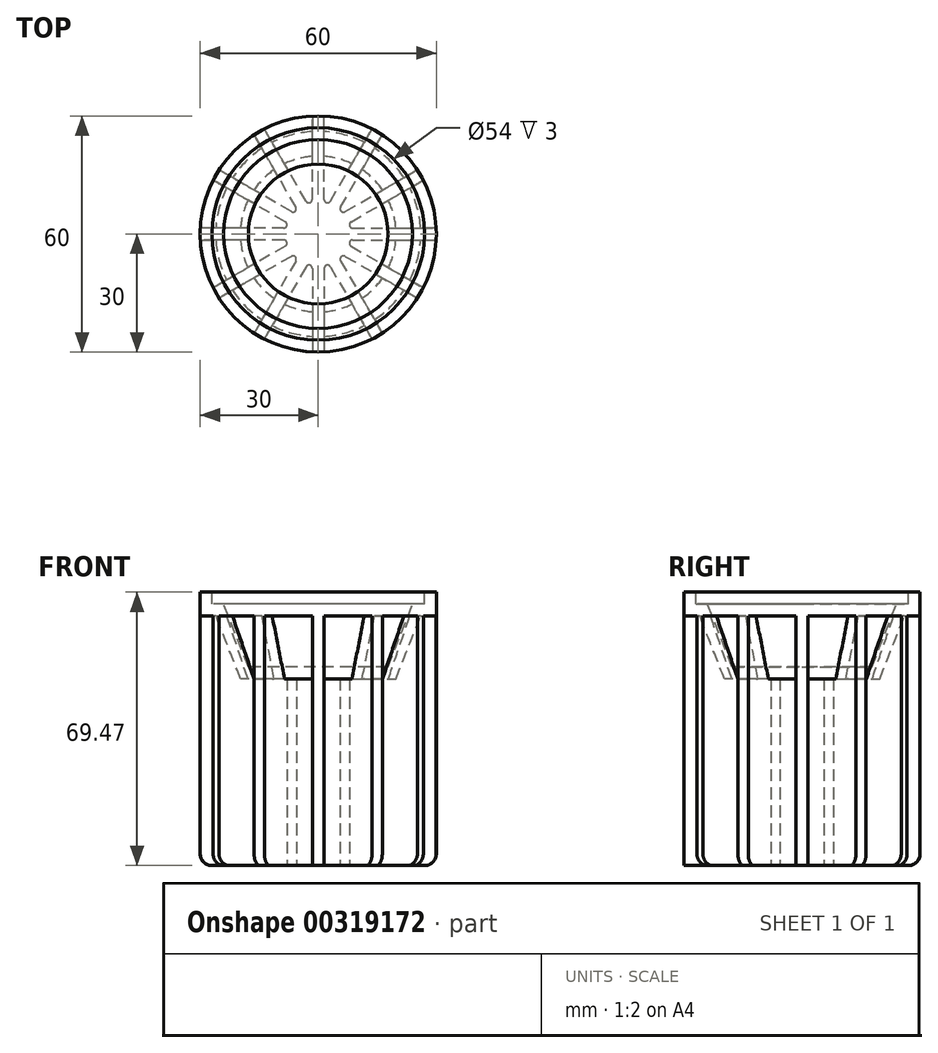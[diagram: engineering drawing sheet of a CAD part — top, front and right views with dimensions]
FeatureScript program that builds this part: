
annotation { "Feature Type Name" : "Feature", "Feature Type Description" : "" }
export const myFeature = defineFeature(function(context is Context, id is Id, definition is map)
    precondition{}
    {
        {
            var Q0;
            Q0=qCreatedBy(makeId("Right.planeOp"),FACE);
            var sketch = newSketch(context, id + "F0", { "sketchPlane" : qUnion([Q0])});
            skLineSegment(sketch, "E0", {"start": v(0, -12.53) * mm, "end": v(-19.8, -12.53) * mm});
            skLineSegment(sketch, "E1", {"start": v(-19.8, -12.53) * mm, "end": v(-26.05, 3.47) * mm});
            skLineSegment(sketch, "E2", {"start": v(-26.05, 3.47) * mm, "end": v(-30, 3.47) * mm});
            skLineSegment(sketch, "E3", {"start": v(-30, 3.47) * mm, "end": v(-30, 9.47) * mm});
            skLineSegment(sketch, "E4", {"start": v(-30, 9.47) * mm, "end": v(-27, 9.47) * mm});
            skLineSegment(sketch, "E5.0", {"start": v(-17.74, -9.53) * mm, "end": v(-24, 6.47) * mm});
            skLineSegment(sketch, "E6.0", {"start": v(0, -9.53) * mm, "end": v(-17.74, -9.53) * mm});
            skLineSegment(sketch, "E7", {"start": v(-24, 6.47) * mm, "end": v(-27, 6.47) * mm});
            skLineSegment(sketch, "E8", {"start": v(-27, 6.47) * mm, "end": v(-27, 9.47) * mm});
            skLineSegment(sketch, "E9", {"start": v(0, -9.53) * mm, "end": v(0, -12.53) * mm});
            skSolve(sketch);
        }
        {
            var Q0;
            Q0 = qSketchRegion(id + "F0", true);
            var Q1;
            Q1=sQuery(id+"F0.wireOp",EDGE,"E9");
            revolve(context, id + "F1", {"entities" : qUnion([Q0]), "axis" : qUnion([Q1]), "revolveType" : RevolveType.FULL});
        }
        {
            var Q0;
            Q0=qCreatedBy(makeId("Top.planeOp"),FACE);
            cPlane(context, id + "F2", {"entities" : qUnion([Q0]), "cplaneType" : CPlaneType.OFFSET, "offset" : 60 * mm, "oppositeDirection" : true, "width" : 150 * mm, "height" : 150 * mm});
        }
        {
            var Q0;
            Q0=qCreatedBy(id+"F2.planeOp",FACE);
            var sketch = newSketch(context, id + "F3", { "sketchPlane" : qUnion([Q0])});
            skCircle(sketch, "E10", {"center": v(0, 0) * mm, "radius": 8.89 * mm, "construction": true});
            skPoint(sketch, "E11.center.orphan", {"position": v(0, -8.89) * mm});
            skPoint(sketch, "E12.center.orphan", {"position": v(0, 8.89) * mm});
            skArc(sketch, "E13", {"start": v(-3.08, -8.34) * mm, "mid": v(-2.13, -7.94) * mm, "end": v(-1.5, -8.76) * mm});
            skArc(sketch, "E14", {"start": v(-5.68, -6.84) * mm, "mid": v(-5.82, -5.82) * mm, "end": v(-6.84, -5.68) * mm});
            skArc(sketch, "E15", {"start": v(-8.76, -1.5) * mm, "mid": v(-7.94, -2.13) * mm, "end": v(-8.34, -3.08) * mm});
            skArc(sketch, "E16.MirrorCS", {"start": v(-8.76, 1.5) * mm, "mid": v(-7.94, 2.13) * mm, "end": v(-8.34, 3.08) * mm});
            skArc(sketch, "E17.MirrorCS", {"start": v(-5.68, 6.84) * mm, "mid": v(-5.82, 5.82) * mm, "end": v(-6.84, 5.68) * mm});
            skArc(sketch, "E18.MirrorCS", {"start": v(-3.08, 8.34) * mm, "mid": v(-2.13, 7.94) * mm, "end": v(-1.5, 8.76) * mm});
            skArc(sketch, "E19.MirrorCS", {"start": v(3.08, -8.34) * mm, "mid": v(2.13, -7.94) * mm, "end": v(1.5, -8.76) * mm});
            skArc(sketch, "E20.MirrorCS", {"start": v(5.68, -6.84) * mm, "mid": v(5.82, -5.82) * mm, "end": v(6.84, -5.68) * mm});
            skArc(sketch, "E21.MirrorCS", {"start": v(8.76, -1.5) * mm, "mid": v(7.94, -2.13) * mm, "end": v(8.34, -3.08) * mm});
            skArc(sketch, "E22.MirrorCS", {"start": v(8.76, 1.5) * mm, "mid": v(7.94, 2.13) * mm, "end": v(8.34, 3.08) * mm});
            skArc(sketch, "E23.MirrorCS", {"start": v(5.68, 6.84) * mm, "mid": v(5.82, 5.82) * mm, "end": v(6.84, 5.68) * mm});
            skArc(sketch, "E24.MirrorCS", {"start": v(3.08, 8.34) * mm, "mid": v(2.13, 7.94) * mm, "end": v(1.5, 8.76) * mm});
            skPoint(sketch, "E25.orphan", {"position": v(-8.76, 1.5) * mm});
            skPoint(sketch, "E26.orphan", {"position": v(-8.34, 3.08) * mm});
            skPoint(sketch, "E27.orphan", {"position": v(-6.84, 5.68) * mm});
            skPoint(sketch, "E28.orphan", {"position": v(-5.68, 6.84) * mm});
            skLineSegment(sketch, "E29", {"start": v(-1.5, -8.76) * mm, "end": v(-1.5, -29.96) * mm});
            skLineSegment(sketch, "E30", {"start": v(1.5, -8.76) * mm, "end": v(1.5, -29.96) * mm});
            skArc(sketch, "E31", {"start": v(-1.5, -29.96) * mm, "mid": v(0, -30) * mm, "end": v(1.5, -29.96) * mm});
            skArc(sketch, "E32.1.0", {"start": v(-16.28, -25.2) * mm, "mid": v(-15, -25.98) * mm, "end": v(-13.68, -26.7) * mm});
            skLineSegment(sketch, "E32.1.1", {"start": v(-5.68, -6.84) * mm, "end": v(-16.28, -25.2) * mm});
            skLineSegment(sketch, "E32.1.2", {"start": v(-3.08, -8.34) * mm, "end": v(-13.68, -26.7) * mm});
            skArc(sketch, "E32.2.0", {"start": v(-26.7, -13.68) * mm, "mid": v(-25.98, -15) * mm, "end": v(-25.2, -16.28) * mm});
            skLineSegment(sketch, "E32.2.1", {"start": v(-8.34, -3.08) * mm, "end": v(-26.7, -13.68) * mm});
            skLineSegment(sketch, "E32.2.2", {"start": v(-6.84, -5.68) * mm, "end": v(-25.2, -16.28) * mm});
            skArc(sketch, "E32.3.0", {"start": v(-29.96, 1.5) * mm, "mid": v(-30, 0) * mm, "end": v(-29.96, -1.5) * mm});
            skLineSegment(sketch, "E32.3.1", {"start": v(-8.76, 1.5) * mm, "end": v(-29.96, 1.5) * mm});
            skLineSegment(sketch, "E32.3.2", {"start": v(-8.76, -1.5) * mm, "end": v(-29.96, -1.5) * mm});
            skLineSegment(sketch, "E33", {"start": v(0, -33.33) * mm, "end": v(0, 31.28) * mm, "construction": true});
            skLineSegment(sketch, "E34", {"start": v(-35.42, 0) * mm, "end": v(33.93, 0) * mm, "construction": true});
            skLineSegment(sketch, "E35.MirrorCS", {"start": v(3.08, -8.34) * mm, "end": v(13.68, -26.7) * mm});
            skLineSegment(sketch, "E36.MirrorCS", {"start": v(5.68, -6.84) * mm, "end": v(16.28, -25.2) * mm});
            skLineSegment(sketch, "E37.MirrorCS", {"start": v(6.84, -5.68) * mm, "end": v(25.2, -16.28) * mm});
            skLineSegment(sketch, "E38.MirrorCS", {"start": v(8.34, -3.08) * mm, "end": v(26.7, -13.68) * mm});
            skLineSegment(sketch, "E39.MirrorCS", {"start": v(8.76, -1.5) * mm, "end": v(29.96, -1.5) * mm});
            skLineSegment(sketch, "E40.MirrorCS", {"start": v(8.76, 1.5) * mm, "end": v(29.96, 1.5) * mm});
            skArc(sketch, "E41.MirrorCS", {"start": v(29.96, 1.5) * mm, "mid": v(30, 0) * mm, "end": v(29.96, -1.5) * mm});
            skArc(sketch, "E42.MirrorCS", {"start": v(26.7, -13.68) * mm, "mid": v(25.98, -15) * mm, "end": v(25.2, -16.28) * mm});
            skArc(sketch, "E43.MirrorCS", {"start": v(16.28, -25.2) * mm, "mid": v(15, -25.98) * mm, "end": v(13.68, -26.7) * mm});
            skArc(sketch, "E44.MirrorCS", {"start": v(1.5, -29.96) * mm, "mid": v(0, -30) * mm, "end": v(-1.5, -29.96) * mm});
            skLineSegment(sketch, "E45.MirrorCS", {"start": v(-8.34, 3.08) * mm, "end": v(-26.7, 13.68) * mm});
            skLineSegment(sketch, "E46.MirrorCS", {"start": v(-6.84, 5.68) * mm, "end": v(-25.2, 16.28) * mm});
            skArc(sketch, "E47.MirrorCS", {"start": v(-26.7, 13.68) * mm, "mid": v(-25.98, 15) * mm, "end": v(-25.2, 16.28) * mm});
            skLineSegment(sketch, "E48.MirrorCS", {"start": v(-5.68, 6.84) * mm, "end": v(-16.28, 25.2) * mm});
            skArc(sketch, "E49.MirrorCS", {"start": v(-16.28, 25.2) * mm, "mid": v(-15, 25.98) * mm, "end": v(-13.68, 26.7) * mm});
            skLineSegment(sketch, "E50.MirrorCS", {"start": v(-3.08, 8.34) * mm, "end": v(-13.68, 26.7) * mm});
            skLineSegment(sketch, "E51.MirrorCS", {"start": v(-1.5, 8.76) * mm, "end": v(-1.5, 29.96) * mm});
            skLineSegment(sketch, "E52.MirrorCS", {"start": v(1.5, 8.76) * mm, "end": v(1.5, 29.96) * mm});
            skArc(sketch, "E53.MirrorCS", {"start": v(1.5, 29.96) * mm, "mid": v(0, 30) * mm, "end": v(-1.5, 29.96) * mm});
            skLineSegment(sketch, "E54.MirrorCS", {"start": v(3.08, 8.34) * mm, "end": v(13.68, 26.7) * mm});
            skLineSegment(sketch, "E55.MirrorCS", {"start": v(5.68, 6.84) * mm, "end": v(16.28, 25.2) * mm});
            skArc(sketch, "E56.MirrorCS", {"start": v(16.28, 25.2) * mm, "mid": v(15, 25.98) * mm, "end": v(13.68, 26.7) * mm});
            skLineSegment(sketch, "E57.MirrorCS", {"start": v(6.84, 5.68) * mm, "end": v(25.2, 16.28) * mm});
            skArc(sketch, "E58.MirrorCS", {"start": v(26.7, 13.68) * mm, "mid": v(25.98, 15) * mm, "end": v(25.2, 16.28) * mm});
            skLineSegment(sketch, "E59.MirrorCS", {"start": v(8.34, 3.08) * mm, "end": v(26.7, 13.68) * mm});
            skSolve(sketch);
        }
        {
            var Q0;
            Q0 = qSketchRegion(id + "F3", true);
            var Q1;
            Q1=makeQuery(id+"F1.opRevolve","SWEPT_BODY",BODY,{"disambiguationData":[OSD([sQuery(id+"F0.wireOp",EDGE,"E0"),sQuery(id+"F0.wireOp",EDGE,"E1"),sQuery(id+"F0.wireOp",EDGE,"E2"),sQuery(id+"F0.wireOp",EDGE,"E3"),sQuery(id+"F0.wireOp",EDGE,"E4"),sQuery(id+"F0.wireOp",EDGE,"E5.0"),sQuery(id+"F0.wireOp",EDGE,"E6.0"),sQuery(id+"F0.wireOp",EDGE,"E7"),sQuery(id+"F0.wireOp",EDGE,"E8"),sQuery(id+"F0.wireOp",EDGE,"E9")])]});
            extrude(context, id + "F4", {"entities" : qUnion([Q0]), "operationType" : NewBodyOperationType.ADD, "endBound" : BoundingType.UP_TO_BODY, "endBoundEntityBody" : qUnion([Q1]), "depth" : 25 * mm});
        }
        {
            var Q0;
            Q0=makeQuery(id+"F4.opExtrude","CAP_EDGE",EDGE,{"disambiguationData":[OSD([sQuery(id+"F3.wireOp",EDGE,"E32.1.0")])],"isStart":true});
            var Q1;
            Q1=makeQuery(id+"F4.opExtrude","CAP_EDGE",EDGE,{"disambiguationData":[OSD([sQuery(id+"F3.wireOp",EDGE,"E32.2.0")])],"isStart":true});
            var Q2;
            Q2=makeQuery(id+"F4.opExtrude","CAP_EDGE",EDGE,{"disambiguationData":[OSD([sQuery(id+"F3.wireOp",EDGE,"E32.3.0")])],"isStart":true});
            var Q3;
            Q3=makeQuery(id+"F4.opExtrude","CAP_EDGE",EDGE,{"disambiguationData":[OSD([sQuery(id+"F3.wireOp",EDGE,"E47.MirrorCS")])],"isStart":true});
            var Q4;
            Q4=makeQuery(id+"F4.opExtrude","CAP_EDGE",EDGE,{"disambiguationData":[OSD([sQuery(id+"F3.wireOp",EDGE,"E49.MirrorCS")])],"isStart":true});
            var Q5;
            Q5=makeQuery(id+"F4.opExtrude","CAP_EDGE",EDGE,{"disambiguationData":[OSD([sQuery(id+"F3.wireOp",EDGE,"E53.MirrorCS")])],"isStart":true});
            var Q6;
            Q6=makeQuery(id+"F4.opExtrude","CAP_EDGE",EDGE,{"disambiguationData":[OSD([sQuery(id+"F3.wireOp",EDGE,"E56.MirrorCS")])],"isStart":true});
            var Q7;
            Q7=makeQuery(id+"F4.opExtrude","CAP_EDGE",EDGE,{"disambiguationData":[OSD([sQuery(id+"F3.wireOp",EDGE,"E58.MirrorCS")])],"isStart":true});
            var Q8;
            Q8=makeQuery(id+"F4.opExtrude","CAP_EDGE",EDGE,{"disambiguationData":[OSD([sQuery(id+"F3.wireOp",EDGE,"E41.MirrorCS")])],"isStart":true});
            var Q9;
            Q9=makeQuery(id+"F4.opExtrude","CAP_EDGE",EDGE,{"disambiguationData":[OSD([sQuery(id+"F3.wireOp",EDGE,"E42.MirrorCS")])],"isStart":true});
            var Q10;
            Q10=makeQuery(id+"F4.opExtrude","CAP_EDGE",EDGE,{"disambiguationData":[OSD([sQuery(id+"F3.wireOp",EDGE,"E43.MirrorCS")])],"isStart":true});
            var Q11;
            Q11=makeQuery(id+"F4.opExtrude","CAP_EDGE",EDGE,{"disambiguationData":[OSD([sQuery(id+"F3.wireOp",EDGE,"E44.MirrorCS")])],"isStart":true});
            fillet(context, id + "F5", {"entities" : qUnion([Q0, Q1, Q2, Q3, Q4, Q5, Q6, Q7, Q8, Q9, Q10, Q11]), "radius" : 3 * mm, "tangentPropagation" : true, "allowEdgeOverflow" : false});
        }
    });
